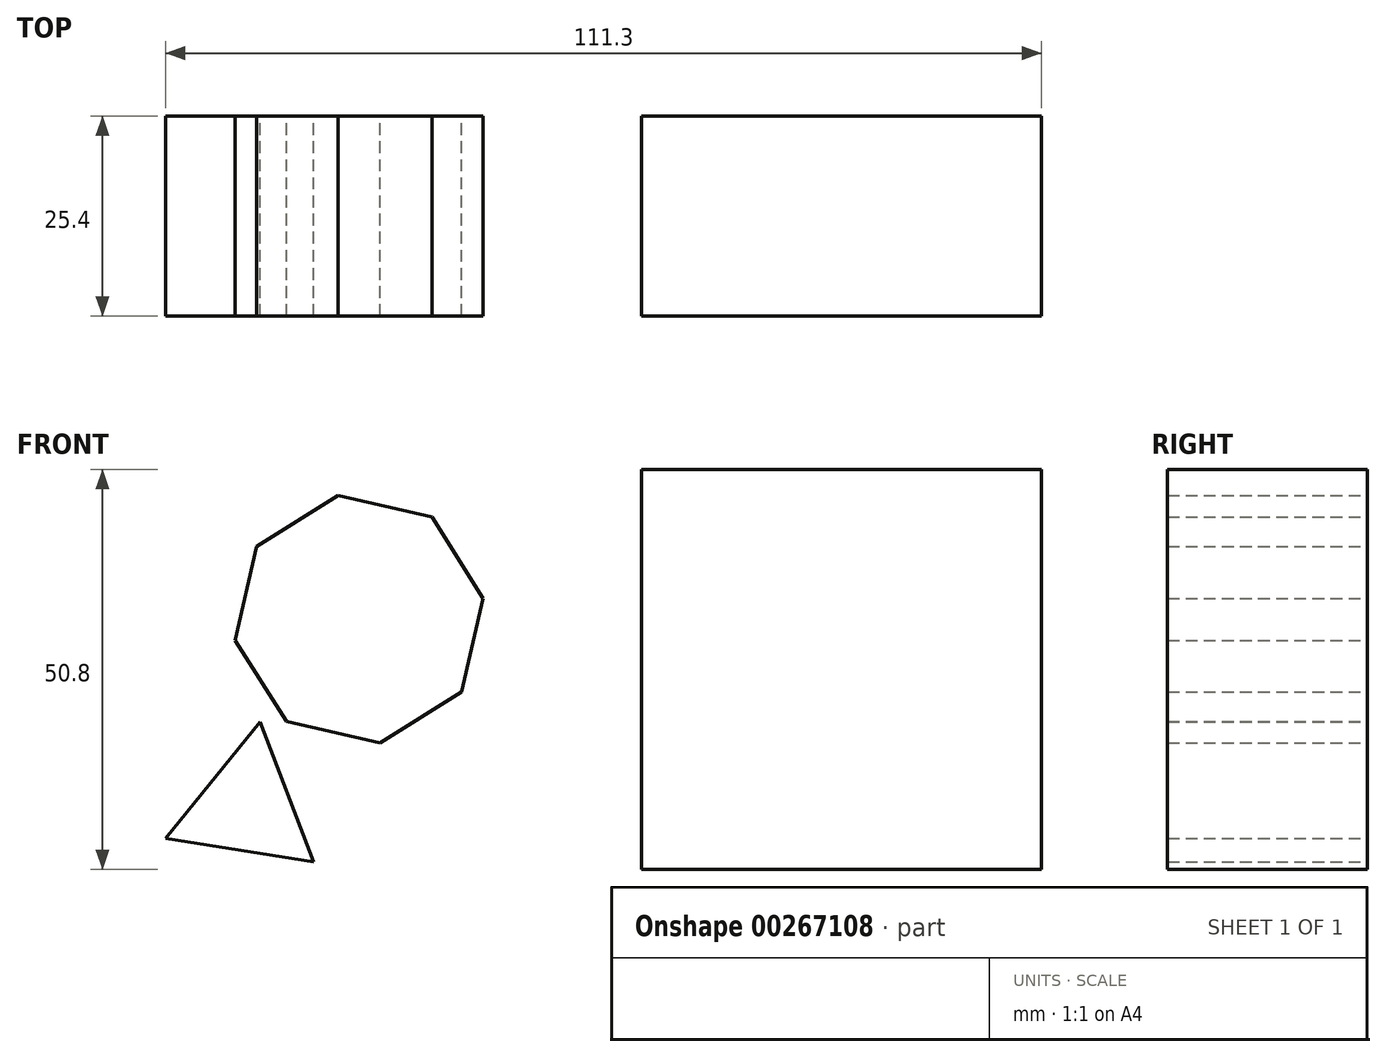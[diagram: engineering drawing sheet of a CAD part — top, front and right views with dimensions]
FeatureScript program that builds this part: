
annotation { "Feature Type Name" : "Feature", "Feature Type Description" : "" }
export const myFeature = defineFeature(function(context is Context, id is Id, definition is map)
    precondition{}
    {
        {
            var Q0;
            Q0=qCreatedBy(makeId("Front.planeOp"),FACE);
            var sketch = newSketch(context, id + "F0", { "sketchPlane" : qUnion([Q0])});
            skLineSegment(sketch, "E0.bottom", {"start": v(-75.4, 63.48) * mm, "end": v(-24.6, 63.48) * mm});
            skLineSegment(sketch, "E0.top", {"start": v(-75.4, 12.68) * mm, "end": v(-24.6, 12.68) * mm});
            skLineSegment(sketch, "E0.left", {"start": v(-75.4, 63.48) * mm, "end": v(-75.4, 12.68) * mm});
            skLineSegment(sketch, "E0.right", {"start": v(-24.6, 63.48) * mm, "end": v(-24.6, 12.68) * mm});
            skCircle(sketch, "E1.cCircle", {"center": v(-42.3, 46.16) * mm, "radius": 15.95 * mm, "construction": true});
            skLineSegment(sketch, "E1.0", {"start": v(-33.05, 59.16) * mm, "end": v(-26.57, 48.82) * mm});
            skLineSegment(sketch, "E1.1", {"start": v(-26.57, 48.82) * mm, "end": v(-29.3, 36.91) * mm});
            skLineSegment(sketch, "E1.2", {"start": v(-29.3, 36.91) * mm, "end": v(-39.65, 30.43) * mm});
            skLineSegment(sketch, "E1.3", {"start": v(-39.65, 30.43) * mm, "end": v(-51.55, 33.16) * mm});
            skLineSegment(sketch, "E1.4", {"start": v(-51.55, 33.16) * mm, "end": v(-58.03, 43.5) * mm});
            skLineSegment(sketch, "E1.5", {"start": v(-58.03, 43.5) * mm, "end": v(-55.3, 55.4) * mm});
            skLineSegment(sketch, "E1.6", {"start": v(-55.3, 55.4) * mm, "end": v(-44.95, 61.9) * mm});
            skLineSegment(sketch, "E1.7", {"start": v(-44.95, 61.9) * mm, "end": v(-33.05, 59.16) * mm});
            skCircle(sketch, "E2.cCircle", {"center": v(-56.63, 22.27) * mm, "radius": 11 * mm, "construction": true});
            skLineSegment(sketch, "E2.0", {"start": v(-48.1, 15.32) * mm, "end": v(-66.91, 18.36) * mm});
            skLineSegment(sketch, "E2.1", {"start": v(-66.91, 18.36) * mm, "end": v(-54.88, 33.13) * mm});
            skLineSegment(sketch, "E2.2", {"start": v(-54.88, 33.13) * mm, "end": v(-48.1, 15.32) * mm});
            skSolve(sketch);
        }
        {
            var Q0;
            Q0=makeQuery(id+"F0.imprint","IMPRINT",FACE,{"disambiguationData":[TD([[makeQuery(id+"F0.imprint","IMPRINT",EDGE,{"derivedFrom":sQuery(id+"F0.wireOp",EDGE,"E1.0")}),-1.0]])]});
            var Q1;
            Q1=makeQuery(id+"F0.imprint","IMPRINT",FACE,{"disambiguationData":[TD([[makeQuery(id+"F0.imprint","IMPRINT",EDGE,{"derivedFrom":sQuery(id+"F0.wireOp",EDGE,"E2.0")}),-1.0]])]});
            extrude(context, id + "F1", {"entities" : qUnion([Q0, Q1]), "depth" : 25.4 * mm});
        }
        {
            var Q0;
            Q0=qCreatedBy(makeId("Front.planeOp"),FACE);
            var sketch = newSketch(context, id + "F2", { "sketchPlane" : qUnion([Q0])});
            skLineSegment(sketch, "E3.bottom", {"start": v(-6.4, 65.19) * mm, "end": v(44.4, 65.19) * mm});
            skLineSegment(sketch, "E3.top", {"start": v(-6.4, 14.39) * mm, "end": v(44.4, 14.39) * mm});
            skLineSegment(sketch, "E3.left", {"start": v(-6.4, 65.19) * mm, "end": v(-6.4, 14.39) * mm});
            skLineSegment(sketch, "E3.right", {"start": v(44.4, 65.19) * mm, "end": v(44.4, 14.39) * mm});
            skSolve(sketch);
        }
        {
            var Q0;
            Q0=makeQuery(id+"F2.imprint","IMPRINT",FACE,{"disambiguationData":[TD([[makeQuery(id+"F2.imprint","IMPRINT",EDGE,{"derivedFrom":sQuery(id+"F2.wireOp",EDGE,"E3.bottom")}),-1.0]])]});
            extrude(context, id + "F3", {"entities" : qUnion([Q0]), "depth" : 25.4 * mm});
        }
    });
